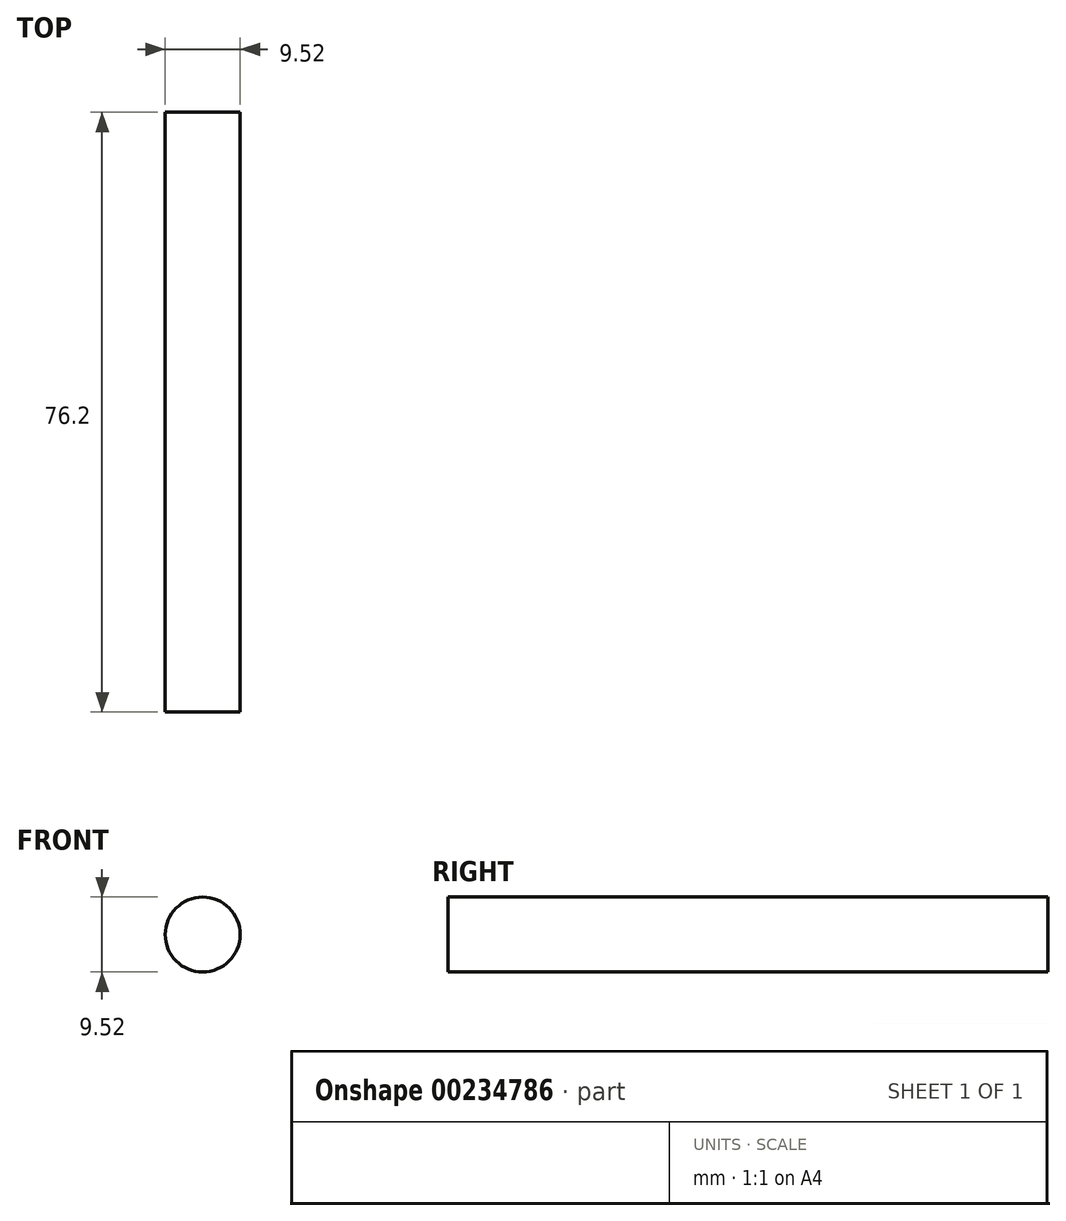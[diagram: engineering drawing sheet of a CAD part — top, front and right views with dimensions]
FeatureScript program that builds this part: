
annotation { "Feature Type Name" : "Feature", "Feature Type Description" : "" }
export const myFeature = defineFeature(function(context is Context, id is Id, definition is map)
    precondition{}
    {
        {
            var Q0;
            Q0=qCreatedBy(makeId("Front.planeOp"),FACE);
            var sketch = newSketch(context, id + "F1", { "sketchPlane" : qUnion([Q0])});
            skCircle(sketch, "E0", {"center": v(0, 0) * mm, "radius": 4.76 * mm});
            skSolve(sketch);
        }
        {
            var Q0;
            Q0=makeQuery(id+"F1.imprint","IMPRINT",FACE,{"disambiguationData":[TD([[makeQuery(id+"F1.imprint","IMPRINT",EDGE,{"derivedFrom":sQuery(id+"F1.wireOp",EDGE,"E0")}),1.0]])]});
            extrude(context, id + "F0", {"entities" : qUnion([Q0]), "depth" : 76.2 * mm});
        }
    });
